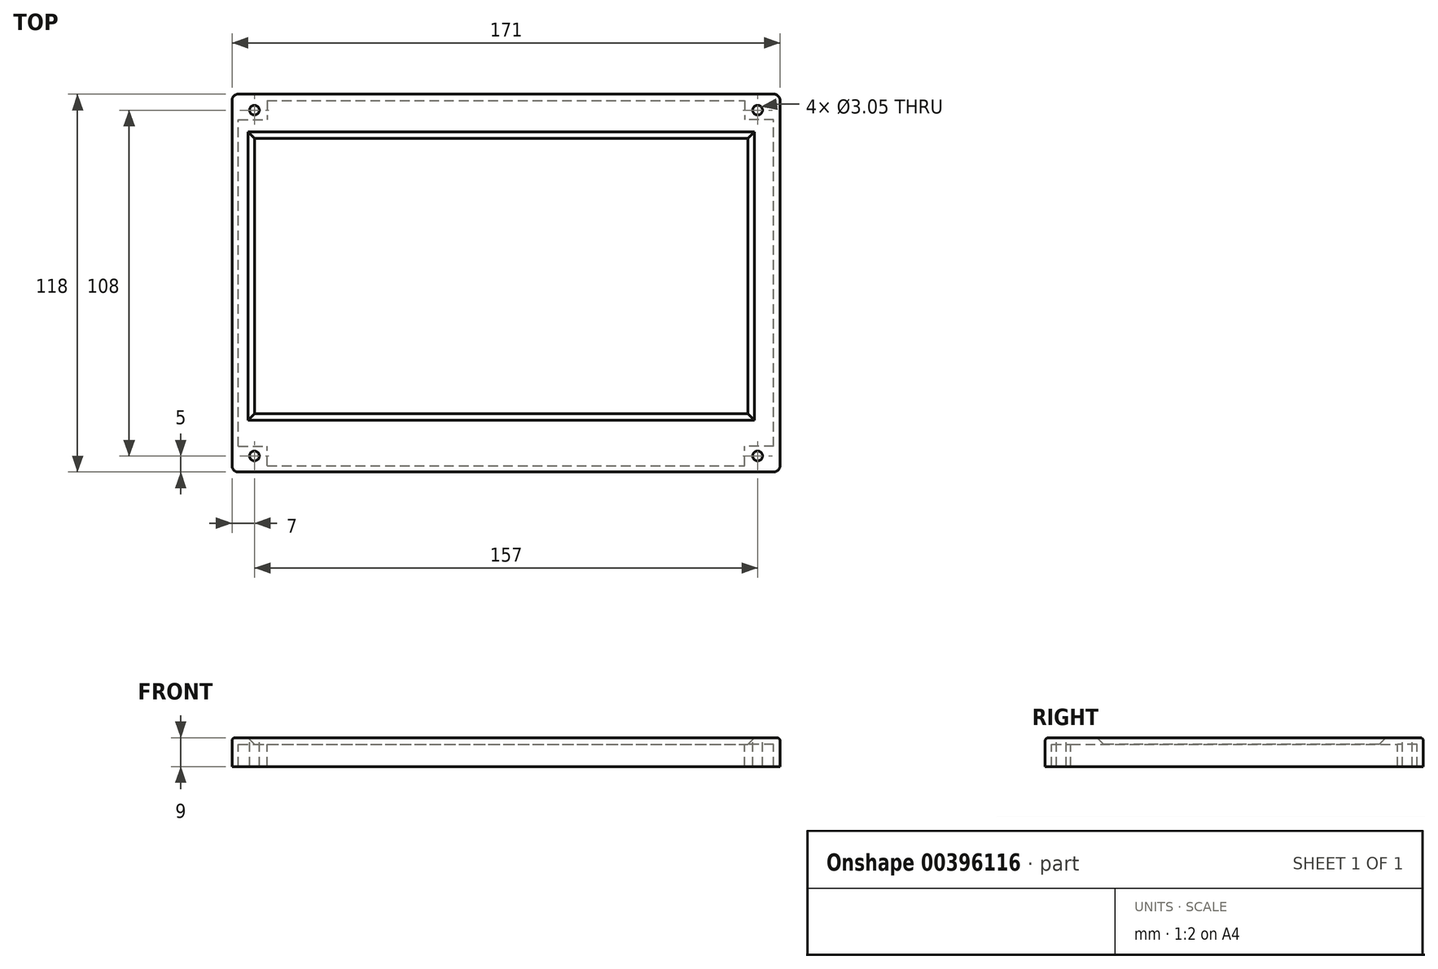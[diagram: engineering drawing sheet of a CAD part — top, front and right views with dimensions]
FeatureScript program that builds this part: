
annotation { "Feature Type Name" : "Feature", "Feature Type Description" : "" }
export const myFeature = defineFeature(function(context is Context, id is Id, definition is map)
    precondition{}
    {
        {
            var Q0;
            Q0=qCreatedBy(makeId("Top.planeOp"),FACE);
            var sketch = newSketch(context, id + "F0", { "sketchPlane" : qUnion([Q0])});
            skLineSegment(sketch, "E0.bottom", {"start": v(-84, 56.74) * mm, "end": v(87, 56.74) * mm});
            skLineSegment(sketch, "E0.top", {"start": v(-84, -61.26) * mm, "end": v(87, -61.26) * mm});
            skLineSegment(sketch, "E0.left", {"start": v(-84, 56.74) * mm, "end": v(-84, -61.26) * mm});
            skLineSegment(sketch, "E0.right", {"start": v(87, 56.74) * mm, "end": v(87, -61.26) * mm});
            skLineSegment(sketch, "E1.bottom", {"start": v(-77, 42.96) * mm, "end": v(77, 42.96) * mm});
            skLineSegment(sketch, "E1.top", {"start": v(-77, -43.04) * mm, "end": v(77, -43.04) * mm});
            skLineSegment(sketch, "E1.left", {"start": v(-77, 42.96) * mm, "end": v(-77, -43.04) * mm});
            skLineSegment(sketch, "E1.right", {"start": v(77, 42.96) * mm, "end": v(77, -43.04) * mm});
            skSolve(sketch);
        }
        {
            var Q0;
            Q0=makeQuery(id+"F0.imprint","IMPRINT",FACE,{"disambiguationData":[TD([[makeQuery(id+"F0.imprint","IMPRINT",EDGE,{"derivedFrom":sQuery(id+"F0.wireOp",EDGE,"E0.bottom")}),-1.0]])]});
            extrude(context, id + "F1", {"entities" : qUnion([Q0]), "depth" : 2 * mm});
        }
        {
            var Q0;
            Q0=makeQuery(id+"F1.opExtrude","CAP_EDGE",EDGE,{"disambiguationData":[OSD([sQuery(id+"F0.wireOp",EDGE,"E1.bottom")])],"isStart":false});
            var Q1;
            Q1=makeQuery(id+"F1.opExtrude","CAP_EDGE",EDGE,{"disambiguationData":[OSD([sQuery(id+"F0.wireOp",EDGE,"E1.right")])],"isStart":false});
            var Q2;
            Q2=makeQuery(id+"F1.opExtrude","CAP_EDGE",EDGE,{"disambiguationData":[OSD([sQuery(id+"F0.wireOp",EDGE,"E1.left")])],"isStart":false});
            var Q3;
            Q3=makeQuery(id+"F1.opExtrude","CAP_EDGE",EDGE,{"disambiguationData":[OSD([sQuery(id+"F0.wireOp",EDGE,"E1.top")])],"isStart":false});
            chamfer(context, id + "F2", {"entities" : qUnion([Q0, Q1, Q2, Q3]), "width" : 2 * mm, "tangentPropagation" : true});
        }
        {
            var Q0;
            Q0=makeQuery(id+"F1.opExtrude","CAP_EDGE",EDGE,{"disambiguationData":[OSD([sQuery(id+"F0.wireOp",EDGE,"E0.top")])],"isStart":false});
            var Q1;
            Q1=makeQuery(id+"F1.opExtrude","CAP_EDGE",EDGE,{"disambiguationData":[OSD([sQuery(id+"F0.wireOp",EDGE,"E0.right")])],"isStart":false});
            var Q2;
            Q2=makeQuery(id+"F1.opExtrude","CAP_EDGE",EDGE,{"disambiguationData":[OSD([sQuery(id+"F0.wireOp",EDGE,"E0.bottom")])],"isStart":false});
            var Q3;
            Q3=makeQuery(id+"F1.opExtrude","CAP_EDGE",EDGE,{"disambiguationData":[OSD([sQuery(id+"F0.wireOp",EDGE,"E0.left")])],"isStart":false});
            fillet(context, id + "F3", {"entities" : qUnion([Q0, Q1, Q2, Q3]), "radius" : 1 * mm, "tangentPropagation" : true, "allowEdgeOverflow" : false});
        }
        {
            var Q0;
            Q0=makeQuery(id+"F1.opExtrude","CAP_FACE",FACE,{"disambiguationData":[OSD([sQuery(id+"F0.wireOp",EDGE,"E0.bottom"),sQuery(id+"F0.wireOp",EDGE,"E0.top"),sQuery(id+"F0.wireOp",EDGE,"E0.left"),sQuery(id+"F0.wireOp",EDGE,"E0.right"),sQuery(id+"F0.wireOp",EDGE,"E1.bottom"),sQuery(id+"F0.wireOp",EDGE,"E1.top"),sQuery(id+"F0.wireOp",EDGE,"E1.left"),sQuery(id+"F0.wireOp",EDGE,"E1.right")])],"isStart":true});
            var sketch = newSketch(context, id + "F4", { "sketchPlane" : qUnion([Q0])});
            skLineSegment(sketch, "E2", {"start": v(-82, 61.26) * mm, "end": v(-82, -56.74) * mm});
            skLineSegment(sketch, "E3", {"start": v(85, 61.26) * mm, "end": v(85, -56.74) * mm});
            skLineSegment(sketch, "E4", {"start": v(-82, 59.26) * mm, "end": v(85, 59.26) * mm});
            skLineSegment(sketch, "E5", {"start": v(-82, -54.74) * mm, "end": v(85, -54.74) * mm});
            skSolve(sketch);
        }
        {
            var Q0;
            {var subQ0=sQuery(id+"F4.wireOp",EDGE,"E2");Q0=makeQuery(id+"F4.imprint","IMPRINT",FACE,{"disambiguationData":[TD([[makeQuery(id+"F4.imprint","IMPRINT",EDGE,{"derivedFrom":subQ0}),-1.0]])]});}
            var Q1;
            {var subQ0=sQuery(id+"F4.wireOp",EDGE,"E3");Q1=makeQuery(id+"F4.imprint","IMPRINT",FACE,{"disambiguationData":[TD([[makeQuery(id+"F4.imprint","IMPRINT",EDGE,{"derivedFrom":subQ0}),1.0]])]});}
            var Q2;
            {var subQ3=sQuery(id+"F4.wireOp",EDGE,"E4");Q2=makeQuery(id+"F4.imprint","IMPRINT",FACE,{"disambiguationData":[TD([[makeQuery(id+"F4.imprint","IMPRINT",EDGE,{"derivedFrom":subQ3}),1.0]])]});}
            var Q3;
            {var subQ3=sQuery(id+"F4.wireOp",EDGE,"E5");Q3=makeQuery(id+"F4.imprint","IMPRINT",FACE,{"disambiguationData":[TD([[makeQuery(id+"F4.imprint","IMPRINT",EDGE,{"derivedFrom":subQ3}),-1.0]])]});}
            extrude(context, id + "F5", {"entities" : qUnion([Q0, Q1, Q2, Q3]), "operationType" : NewBodyOperationType.ADD, "depth" : 7 * mm});
        }
        {
            var Q0;
            Q0=makeQuery(id+"F1.opExtrude","CAP_FACE",FACE,{"disambiguationData":[OSD([sQuery(id+"F0.wireOp",EDGE,"E0.bottom"),sQuery(id+"F0.wireOp",EDGE,"E0.top"),sQuery(id+"F0.wireOp",EDGE,"E0.left"),sQuery(id+"F0.wireOp",EDGE,"E0.right"),sQuery(id+"F0.wireOp",EDGE,"E1.bottom"),sQuery(id+"F0.wireOp",EDGE,"E1.top"),sQuery(id+"F0.wireOp",EDGE,"E1.left"),sQuery(id+"F0.wireOp",EDGE,"E1.right")])],"isStart":true});
            var sketch = newSketch(context, id + "F6", { "sketchPlane" : qUnion([Q0])});
            skLineSegment(sketch, "E6.bottom", {"start": v(-82, 59.26) * mm, "end": v(-73, 59.26) * mm});
            skLineSegment(sketch, "E6.top", {"start": v(-82, 53.26) * mm, "end": v(-73, 53.26) * mm});
            skLineSegment(sketch, "E6.left", {"start": v(-82, 59.26) * mm, "end": v(-82, 53.26) * mm});
            skLineSegment(sketch, "E6.right", {"start": v(-73, 59.26) * mm, "end": v(-73, 53.26) * mm});
            skLineSegment(sketch, "E7.bottom", {"start": v(85, 59.26) * mm, "end": v(76, 59.26) * mm});
            skLineSegment(sketch, "E7.top", {"start": v(85, 53.26) * mm, "end": v(76, 53.26) * mm});
            skLineSegment(sketch, "E7.left", {"start": v(85, 59.26) * mm, "end": v(85, 53.26) * mm});
            skLineSegment(sketch, "E7.right", {"start": v(76, 59.26) * mm, "end": v(76, 53.26) * mm});
            skLineSegment(sketch, "E8.bottom", {"start": v(85, -54.74) * mm, "end": v(76, -54.74) * mm});
            skLineSegment(sketch, "E8.top", {"start": v(85, -48.74) * mm, "end": v(76, -48.74) * mm});
            skLineSegment(sketch, "E8.left", {"start": v(85, -54.74) * mm, "end": v(85, -48.74) * mm});
            skLineSegment(sketch, "E8.right", {"start": v(76, -54.74) * mm, "end": v(76, -48.74) * mm});
            skLineSegment(sketch, "E9.bottom", {"start": v(-82, -54.74) * mm, "end": v(-73, -54.74) * mm});
            skLineSegment(sketch, "E9.top", {"start": v(-82, -48.74) * mm, "end": v(-73, -48.74) * mm});
            skLineSegment(sketch, "E9.left", {"start": v(-82, -54.74) * mm, "end": v(-82, -48.74) * mm});
            skLineSegment(sketch, "E9.right", {"start": v(-73, -54.74) * mm, "end": v(-73, -48.74) * mm});
            skSolve(sketch);
        }
        {
            var Q0;
            Q0 = qSketchRegion(id + "F6", true);
            extrude(context, id + "F7", {"entities" : qUnion([Q0]), "operationType" : NewBodyOperationType.ADD, "depth" : 7 * mm});
        }
        {
            var Q0;
            Q0=makeQuery(id+"F1.opExtrude","CAP_FACE",FACE,{"disambiguationData":[OSD([sQuery(id+"F0.wireOp",EDGE,"E0.bottom"),sQuery(id+"F0.wireOp",EDGE,"E0.top"),sQuery(id+"F0.wireOp",EDGE,"E0.left"),sQuery(id+"F0.wireOp",EDGE,"E0.right"),sQuery(id+"F0.wireOp",EDGE,"E1.bottom"),sQuery(id+"F0.wireOp",EDGE,"E1.top"),sQuery(id+"F0.wireOp",EDGE,"E1.left"),sQuery(id+"F0.wireOp",EDGE,"E1.right")])],"isStart":false});
            var sketch = newSketch(context, id + "F8", { "sketchPlane" : qUnion([Q0])});
            skCircle(sketch, "E10", {"center": v(-77, 51.74) * mm, "radius": 1.53 * mm});
            skCircle(sketch, "E11", {"center": v(80, 51.74) * mm, "radius": 1.52 * mm});
            skCircle(sketch, "E12", {"center": v(80, -56.26) * mm, "radius": 1.52 * mm});
            skCircle(sketch, "E13", {"center": v(-77, -56.26) * mm, "radius": 1.53 * mm});
            skSolve(sketch);
        }
        {
            var Q0;
            Q0 = qSketchRegion(id + "F8", true);
            extrude(context, id + "F9", {"entities" : qUnion([Q0]), "operationType" : NewBodyOperationType.REMOVE, "endBound" : BoundingType.THROUGH_ALL, "oppositeDirection" : true, "depth" : 25 * mm});
        }
        {
            var Q0;
            {var subQ0=sQuery(id+"F0.wireOp",EDGE,"E0.left");var subQ1=sQuery(id+"F0.wireOp",EDGE,"E0.bottom");Q0=makeQuery(id+"F5.boolean.opBoolean","MERGE",EDGE,{"derivedFrom":[makeQuery(id+"F1.opExtrude","SWEPT_EDGE",EDGE,{"disambiguationData":[OSD([subQ1,subQ0])]}),makeQuery(id+"F5.opExtrude","SWEPT_EDGE",EDGE,{"disambiguationData":[OSD([subQ1,subQ0])]})]});}
            var Q1;
            {var subQ0=sQuery(id+"F0.wireOp",EDGE,"E0.right");var subQ1=sQuery(id+"F0.wireOp",EDGE,"E0.bottom");Q1=makeQuery(id+"F5.boolean.opBoolean","MERGE",EDGE,{"derivedFrom":[makeQuery(id+"F1.opExtrude","SWEPT_EDGE",EDGE,{"disambiguationData":[OSD([subQ1,subQ0])]}),makeQuery(id+"F5.opExtrude","SWEPT_EDGE",EDGE,{"disambiguationData":[OSD([subQ1,subQ0])]})]});}
            var Q2;
            {var subQ0=sQuery(id+"F0.wireOp",EDGE,"E0.right");var subQ1=sQuery(id+"F0.wireOp",EDGE,"E0.top");Q2=makeQuery(id+"F5.boolean.opBoolean","MERGE",EDGE,{"derivedFrom":[makeQuery(id+"F1.opExtrude","SWEPT_EDGE",EDGE,{"disambiguationData":[OSD([subQ1,subQ0])]}),makeQuery(id+"F5.opExtrude","SWEPT_EDGE",EDGE,{"disambiguationData":[OSD([subQ1,subQ0])]})]});}
            var Q3;
            {var subQ0=sQuery(id+"F0.wireOp",EDGE,"E0.left");var subQ1=sQuery(id+"F0.wireOp",EDGE,"E0.top");Q3=makeQuery(id+"F5.boolean.opBoolean","MERGE",EDGE,{"derivedFrom":[makeQuery(id+"F1.opExtrude","SWEPT_EDGE",EDGE,{"disambiguationData":[OSD([subQ1,subQ0])]}),makeQuery(id+"F5.opExtrude","SWEPT_EDGE",EDGE,{"disambiguationData":[OSD([subQ1,subQ0])]})]});}
            fillet(context, id + "F10", {"entities" : qUnion([Q0, Q1, Q2, Q3]), "radius" : 2 * mm, "tangentPropagation" : true, "allowEdgeOverflow" : false});
        }
    });
